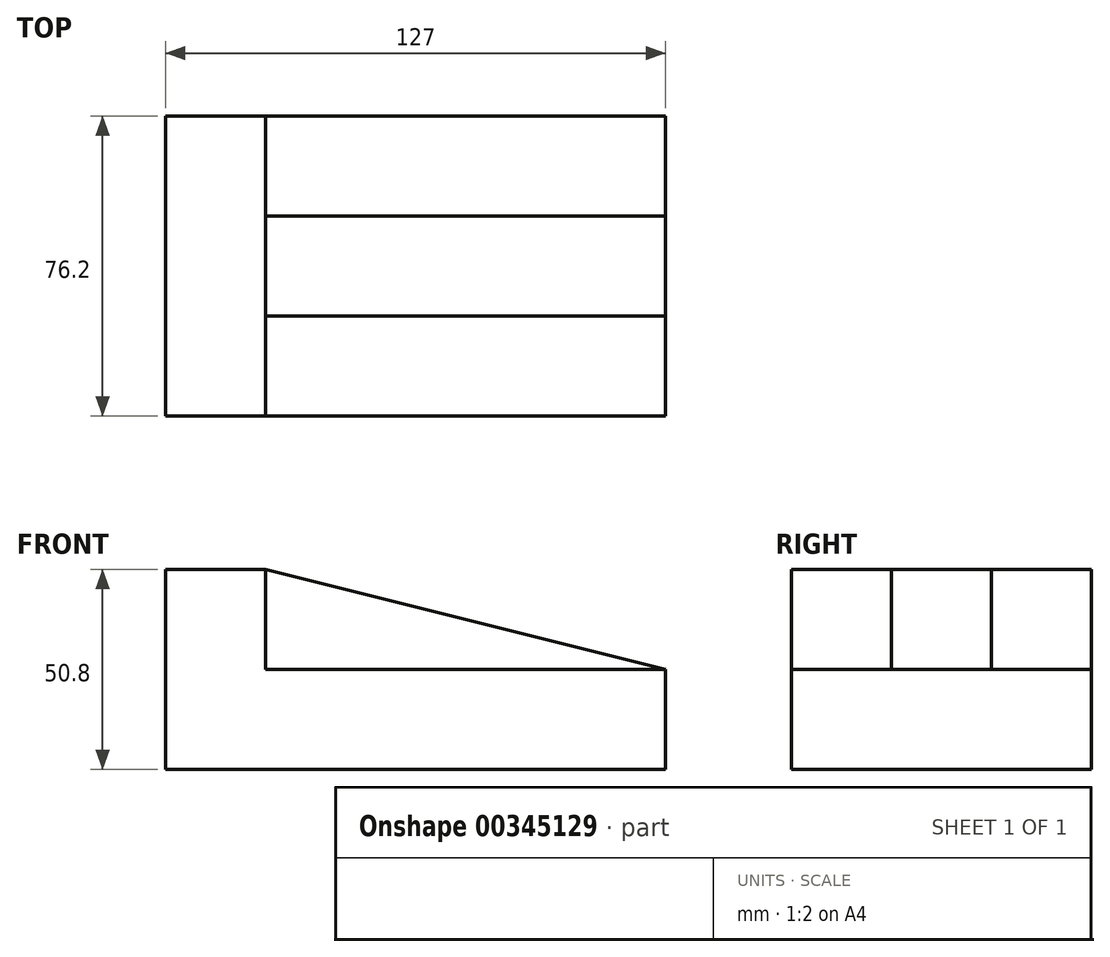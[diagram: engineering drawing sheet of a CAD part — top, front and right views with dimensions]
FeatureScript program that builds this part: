
annotation { "Feature Type Name" : "Feature", "Feature Type Description" : "" }
export const myFeature = defineFeature(function(context is Context, id is Id, definition is map)
    precondition{}
    {
        {
            var Q0;
            Q0=qCreatedBy(makeId("Front.planeOp"),FACE);
            var sketch = newSketch(context, id + "F0", { "sketchPlane" : qUnion([Q0])});
            skLineSegment(sketch, "E0", {"start": v(0, 0) * mm, "end": v(0, 50.8) * mm});
            skLineSegment(sketch, "E1", {"start": v(0, 50.8) * mm, "end": v(25.4, 50.8) * mm});
            skLineSegment(sketch, "E2", {"start": v(25.4, 50.8) * mm, "end": v(127, 25.4) * mm});
            skLineSegment(sketch, "E3", {"start": v(127, 25.4) * mm, "end": v(127, 0) * mm});
            skLineSegment(sketch, "E4", {"start": v(127, 0) * mm, "end": v(0, 0) * mm});
            skSolve(sketch);
        }
        {
            var Q0;
            Q0 = qSketchRegion(id + "F0", true);
            extrude(context, id + "F1", {"entities" : qUnion([Q0]), "depth" : 76.2 * mm});
        }
        {
            var Q0;
            Q0=makeQuery(id+"F1.opExtrude","SWEPT_FACE",FACE,{"disambiguationData":[OSD([sQuery(id+"F0.wireOp",EDGE,"E3")])]});
            var sketch = newSketch(context, id + "F2", { "sketchPlane" : qUnion([Q0])});
            skLineSegment(sketch, "E5.bottom", {"start": v(-76.2, 25.4) * mm, "end": v(-50.8, 25.4) * mm});
            skLineSegment(sketch, "E5.top", {"start": v(-76.2, 50.8) * mm, "end": v(-50.8, 50.8) * mm});
            skLineSegment(sketch, "E5.left", {"start": v(-76.2, 25.4) * mm, "end": v(-76.2, 50.8) * mm});
            skLineSegment(sketch, "E5.right", {"start": v(-50.8, 25.4) * mm, "end": v(-50.8, 50.8) * mm});
            skLineSegment(sketch, "E6.bottom", {"start": v(0, 25.4) * mm, "end": v(-25.4, 25.4) * mm});
            skLineSegment(sketch, "E6.top", {"start": v(0, 50.8) * mm, "end": v(-25.4, 50.8) * mm});
            skLineSegment(sketch, "E6.left", {"start": v(0, 25.4) * mm, "end": v(0, 50.8) * mm});
            skLineSegment(sketch, "E6.right", {"start": v(-25.4, 25.4) * mm, "end": v(-25.4, 50.8) * mm});
            skSolve(sketch);
        }
        {
            var Q0;
            Q0 = qSketchRegion(id + "F2", true);
            extrude(context, id + "F3", {"entities" : qUnion([Q0]), "operationType" : NewBodyOperationType.REMOVE, "oppositeDirection" : true, "depth" : 101.6 * mm});
        }
    });
